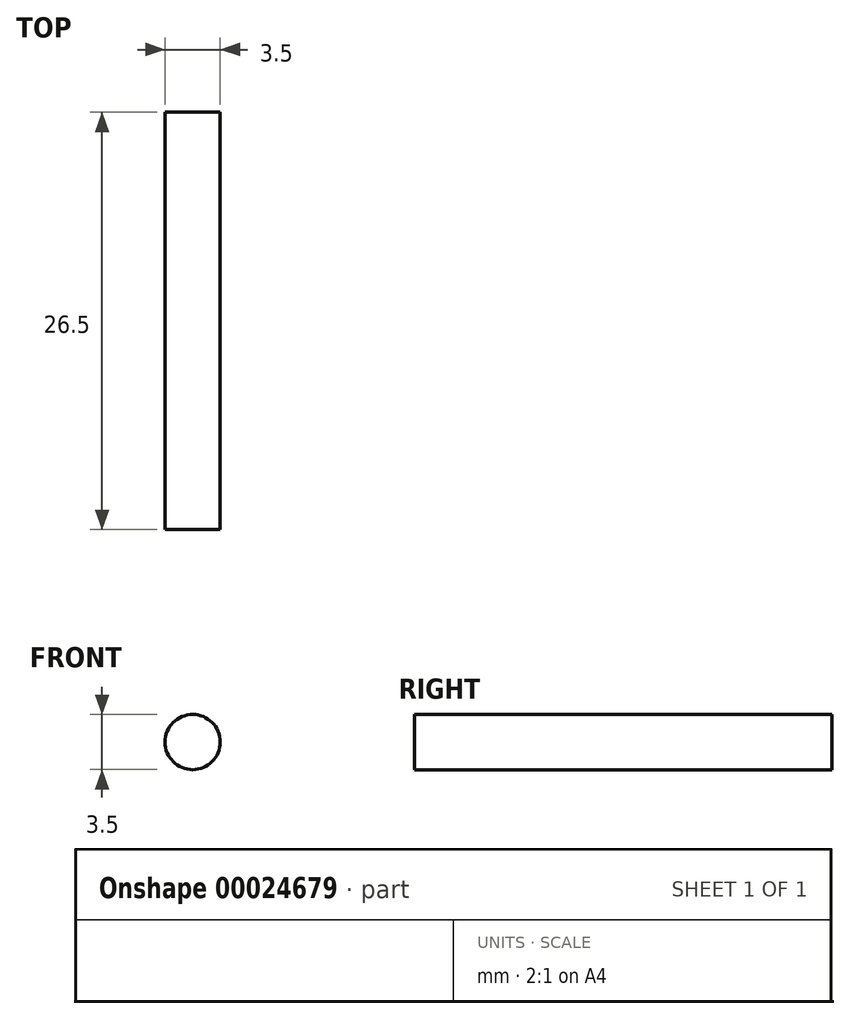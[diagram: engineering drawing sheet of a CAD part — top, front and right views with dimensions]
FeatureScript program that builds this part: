
annotation { "Feature Type Name" : "Feature", "Feature Type Description" : "" }
export const myFeature = defineFeature(function(context is Context, id is Id, definition is map)
    precondition{}
    {
        {
            var Q0;
            Q0=qCreatedBy(makeId("Front.planeOp"),FACE);
            var sketch = newSketch(context, id + "F0", { "sketchPlane" : qUnion([Q0])});
            skCircle(sketch, "E0", {"center": v(0, 0) * mm, "radius": 1.75 * mm});
            skSolve(sketch);
        }
        {
            var Q0;
            Q0=makeQuery(id+"F0.imprint","IMPRINT",FACE,{"disambiguationData":[TD([[makeQuery(id+"F0.imprint","IMPRINT",EDGE,{"derivedFrom":sQuery(id+"F0.wireOp",EDGE,"E0")}),1.0]])]});
            extrude(context, id + "F1", {"entities" : qUnion([Q0]), "depth" : 26.5 * mm});
        }
    });
